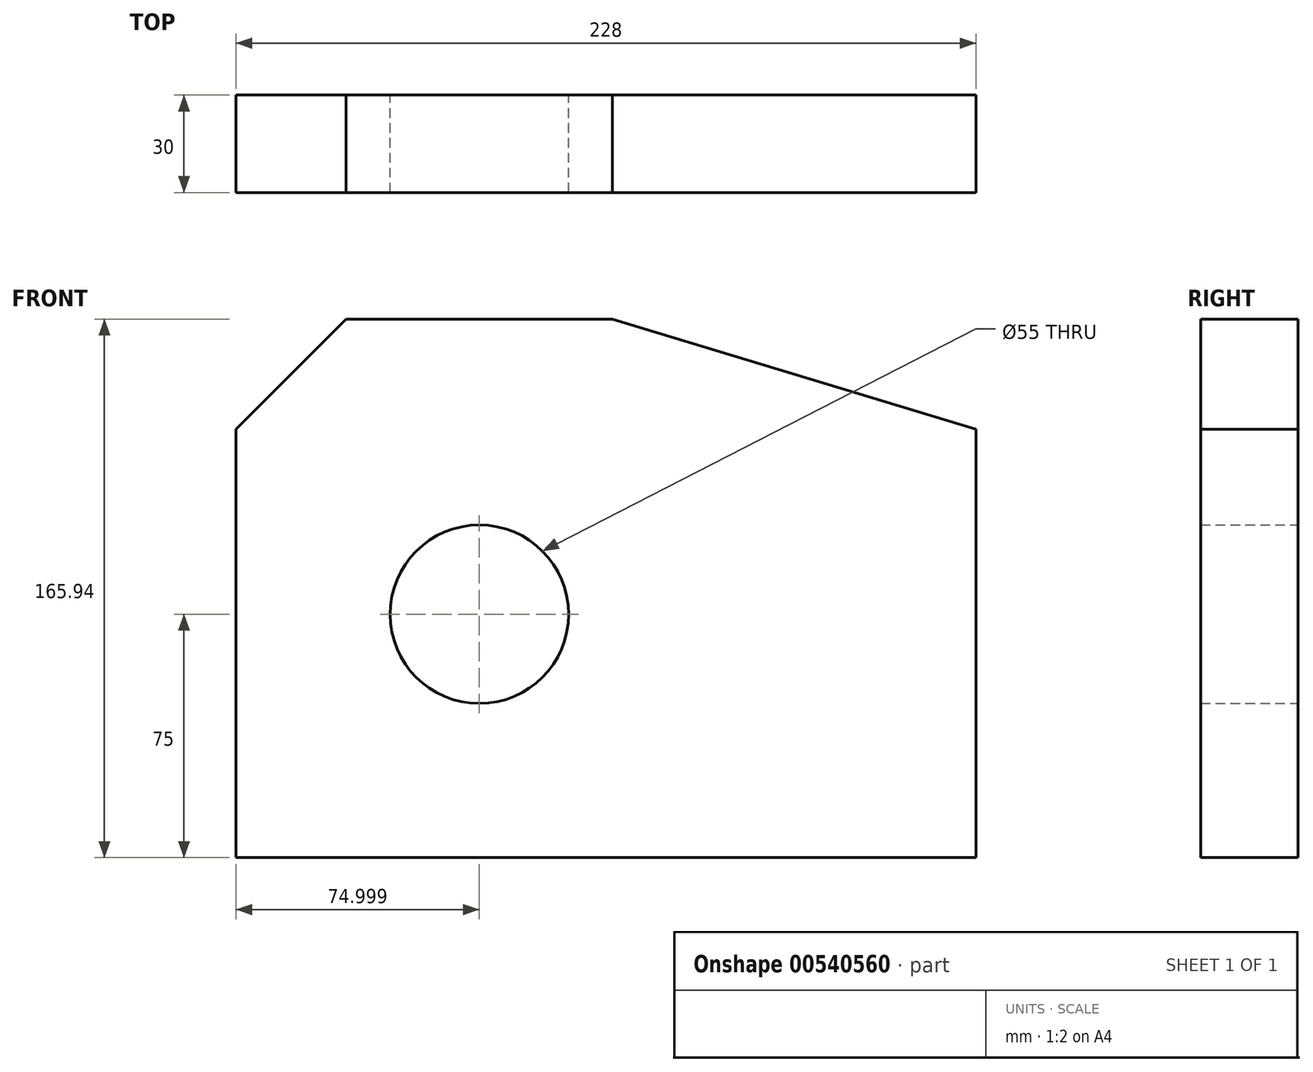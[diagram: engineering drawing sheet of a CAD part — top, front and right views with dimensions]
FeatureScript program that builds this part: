
annotation { "Feature Type Name" : "Feature", "Feature Type Description" : "" }
export const myFeature = defineFeature(function(context is Context, id is Id, definition is map)
    precondition{}
    {
        {
            var Q0;
            Q0=qCreatedBy(makeId("Front.planeOp"),FACE);
            var sketch = newSketch(context, id + "F0", { "sketchPlane" : qUnion([Q0])});
            skLineSegment(sketch, "E0", {"start": v(-33.94, 57) * mm, "end": v(-33.94, -75) * mm});
            skLineSegment(sketch, "E1", {"start": v(-33.94, -75) * mm, "end": v(194.06, -75) * mm});
            skLineSegment(sketch, "E2", {"start": v(194.06, 57) * mm, "end": v(194.06, -75) * mm});
            skLineSegment(sketch, "E3", {"start": v(194.06, 57) * mm, "end": v(82.1, 90.94) * mm});
            skLineSegment(sketch, "E4", {"start": v(0, 90.94) * mm, "end": v(82.1, 90.94) * mm});
            skLineSegment(sketch, "E5", {"start": v(0, 90.94) * mm, "end": v(-33.94, 57) * mm});
            skCircle(sketch, "E6", {"center": v(41.06, 0) * mm, "radius": 27.5 * mm});
            skSolve(sketch);
        }
        {
            var Q0;
            Q0 = qSketchRegion(id + "F0", true);
            extrude(context, id + "F1", {"entities" : qUnion([Q0]), "depth" : 30 * mm, "offsetDistance" : 25 * mm});
        }
    });
